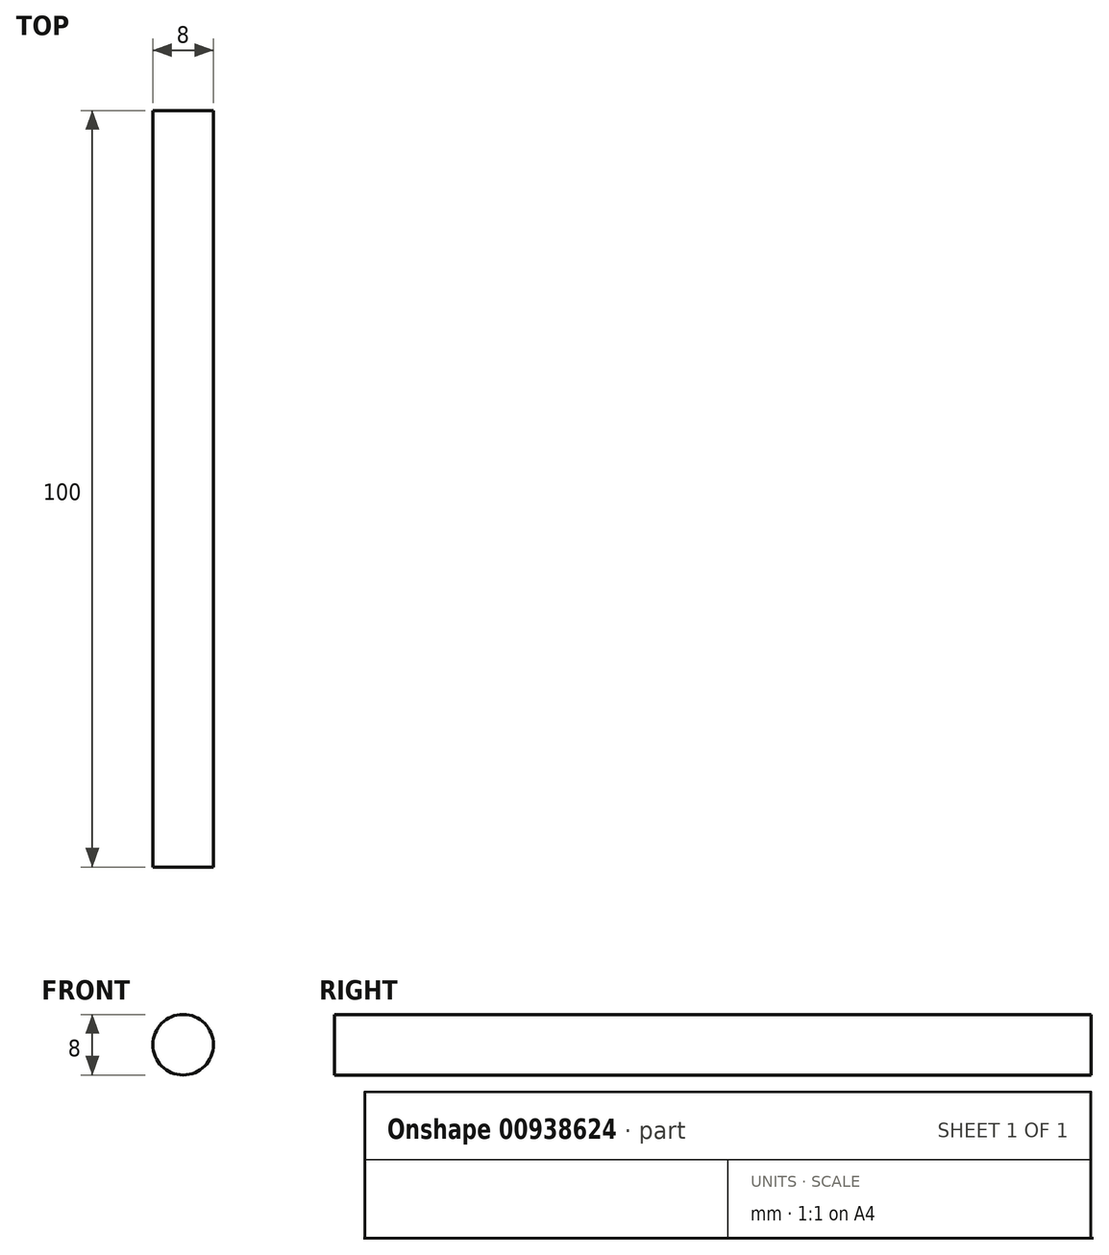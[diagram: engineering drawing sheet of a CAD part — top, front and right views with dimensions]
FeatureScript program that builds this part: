
annotation { "Feature Type Name" : "Feature", "Feature Type Description" : "" }
export const myFeature = defineFeature(function(context is Context, id is Id, definition is map)
    precondition{}
    {
        {
            var Q0;
            Q0=qCreatedBy(makeId("Front.planeOp"),FACE);
            var sketch = newSketch(context, id + "F0", { "sketchPlane" : qUnion([Q0])});
            skCircle(sketch, "E0", {"center": v(0, 0) * mm, "radius": 4 * mm});
            skSolve(sketch);
        }
        {
            var Q0;
            Q0=makeQuery(id+"F0.imprint","IMPRINT",FACE,{"disambiguationData":[TD([[makeQuery(id+"F0.imprint","IMPRINT",EDGE,{"derivedFrom":sQuery(id+"F0.wireOp",EDGE,"E0")}),1.0]])]});
            extrude(context, id + "F1", {"entities" : qUnion([Q0]), "depth" : 100 * mm, "offsetDistance" : 25 * mm});
        }
    });
